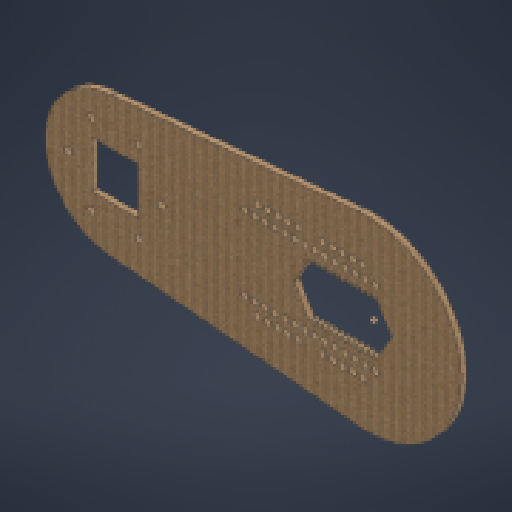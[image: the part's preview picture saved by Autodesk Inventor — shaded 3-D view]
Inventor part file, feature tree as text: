
AUTODESK INVENTOR PART (.ipt)
format: ipt  version: 2024.1 (Build 281209000, 209)  size: 372,224 bytes
history: native  units: in
note: dims shown in document units (in); Inventor stores cm internally (conversion verified against a paired STEP export)
features: other x4, extrude x2, sketch x2, reference x1
ambient origin geometry x8: Origin, YZ Plane, XZ Plane, XY Plane, X Axis, Y Axis, Z Axis, Center Point
bodies: Solid1 (feature_tree)
feature tree (9):
  extrude  "Extrusion1"  Depth=4.0in
  other  "Work Point1"
  extrude  "Extrusion2"  Depth=1.0in
  sketch  "Sketch1"  dims[d0=5.4134in d1=4.0in]
  reference  "Reference1"
  sketch  "Sketch2"  dims[d2=4.3307in d3=1.0in d4=0.1083in d5=60.0deg d6=0.1083in d7=60.0deg d8=0.1083in d9=2.7559in d11=0.2165in d12=0.3937in d14=1.0in d16=0.125in d17=0.0in d18=3.937in d20=0.1083in d21=0.3937in d23=1.0in d25=0.1575in d26=0.1575in d27=0.1575in d28=0.1575in d29=0.1575in d30=0.1575in d31=0.1575in d32=0.1575in d33=0.1575in d34=0.1575in d35=0.1575in d36=0.1575in d37=0.1575in d38=0.1575in d39=0.1575in d40=0.1575in d41=0.1575in d42=0.1575in d43=0.1575in d44=0.1575in d45=0.1575in d46=0.1575in d47=0.1575in d48=0.1575in d49=0.0in d50=0.0in]
  other  "<userpath>\Documents\School\FallCAD\Trebuchet\Trebuchet.iam"
  other  "Trebuchet.iam"
  other  "MainArm:1"
